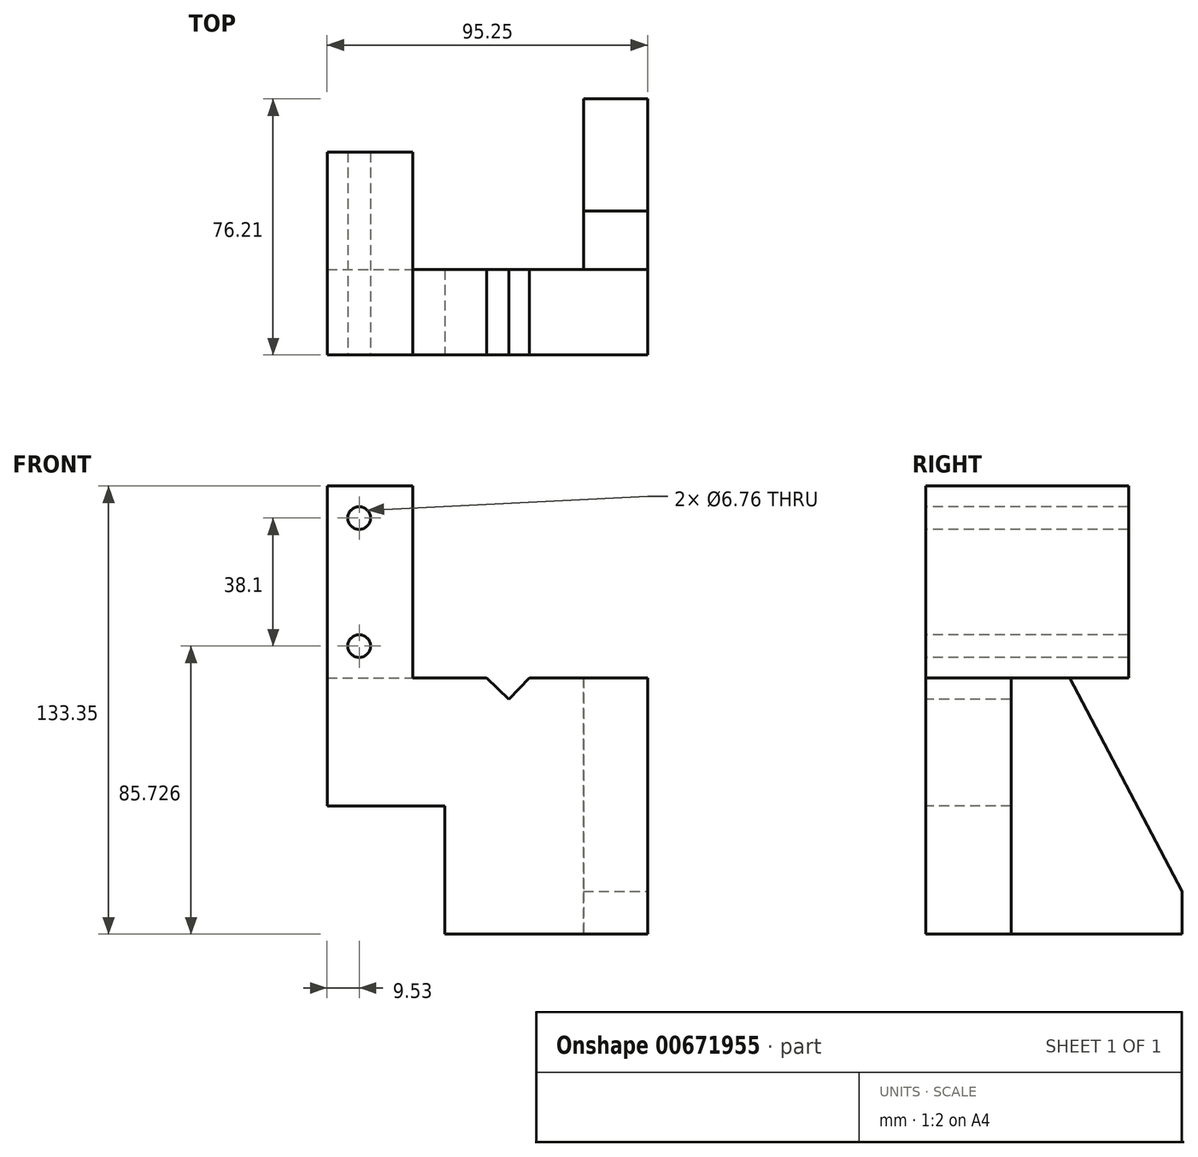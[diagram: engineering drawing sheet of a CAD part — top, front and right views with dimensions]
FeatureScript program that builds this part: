
annotation { "Feature Type Name" : "Feature", "Feature Type Description" : "" }
export const myFeature = defineFeature(function(context is Context, id is Id, definition is map)
    precondition{}
    {
        {
            var Q0;
            Q0=qCreatedBy(makeId("Front.planeOp"),FACE);
            var sketch = newSketch(context, id + "F0", { "sketchPlane" : qUnion([Q0])});
            skLineSegment(sketch, "E0.bottom", {"start": v(-9.53, 39.03) * mm, "end": v(15.87, 39.03) * mm});
            skLineSegment(sketch, "E0.top", {"start": v(-9.52, -18.12) * mm, "end": v(15.88, -18.12) * mm});
            skLineSegment(sketch, "E0.left", {"start": v(-9.53, 39.03) * mm, "end": v(-9.52, -18.12) * mm});
            skLineSegment(sketch, "E0.right", {"start": v(15.87, 39.03) * mm, "end": v(15.88, -18.12) * mm});
            skSolve(sketch);
        }
        {
            var Q0;
            Q0 = qSketchRegion(id + "F0", true);
            extrude(context, id + "F1", {"entities" : qUnion([Q0]), "depth" : 60.32 * mm, "offsetDistance" : 25.4 * mm});
        }
        {
            var Q0;
            Q0=makeQuery(id+"F1.opExtrude","CAP_FACE",FACE,{"disambiguationData":[OSD([sQuery(id+"F0.wireOp",EDGE,"E0.bottom"),sQuery(id+"F0.wireOp",EDGE,"E0.top"),sQuery(id+"F0.wireOp",EDGE,"E0.left"),sQuery(id+"F0.wireOp",EDGE,"E0.right")])],"isStart":false});
            var sketch = newSketch(context, id + "F2", { "sketchPlane" : qUnion([Q0])});
            skPoint(sketch, "E1", {"position": v(0, 29.5) * mm});
            skPoint(sketch, "E2", {"position": v(0, -8.6) * mm});
            skSolve(sketch);
        }
        {
            var Q0;
            Q0=sQuery(id+"F2.wireOp",VERTEX,"E1");
            var Q1;
            Q1=makeQuery(id+"F1.opExtrude","SWEPT_BODY",BODY,{"disambiguationData":[OSD([sQuery(id+"F0.wireOp",EDGE,"E0.bottom"),sQuery(id+"F0.wireOp",EDGE,"E0.top"),sQuery(id+"F0.wireOp",EDGE,"E0.left"),sQuery(id+"F0.wireOp",EDGE,"E0.right")])]});
            hole(context, id + "F3", {"style" : HoleStyle.SIMPLE, "endStyle" : HoleEndStyle.THROUGH, "standardTappedOrClearance" : lookupTablePath({ "standard" : "ANSI", "fit" : "Normal (ASME)", "engagement" : "75%", "pitch" : "20 tpi", "size" : "1/4", "type" : "Clearance" }), "standardBlindInLast" : lookupTablePath({ "fit" : "Free", "standard" : "ANSI", "engagement" : "75%", "pitch" : "20 tpi", "size" : "1/4", "type" : "Clearance" }), "holeDiameter" : 6.76 * mm, "majorDiameter" : 6.35 * mm, "showTappedDepth" : true, "isTappedThrough" : true, "tappedDepth" : 12.7 * mm, "tapClearance" : 3, "locations" : qUnion([Q0]), "scope" : qUnion([Q1])});
        }
        {
            var Q0;
            Q0=makeQuery(id+"F1.opExtrude","CAP_FACE",FACE,{"disambiguationData":[OSD([sQuery(id+"F0.wireOp",EDGE,"E0.bottom"),sQuery(id+"F0.wireOp",EDGE,"E0.top"),sQuery(id+"F0.wireOp",EDGE,"E0.left"),sQuery(id+"F0.wireOp",EDGE,"E0.right")])],"isStart":false});
            var sketch = newSketch(context, id + "F4", { "sketchPlane" : qUnion([Q0])});
            skPoint(sketch, "E3", {"position": v(0, -8.6) * mm});
            skSolve(sketch);
        }
        {
            var Q0;
            Q0=sQuery(id+"F4.wireOp",VERTEX,"E3");
            var Q1;
            Q1=makeQuery(id+"F1.opExtrude","SWEPT_BODY",BODY,{"disambiguationData":[OSD([sQuery(id+"F0.wireOp",EDGE,"E0.bottom"),sQuery(id+"F0.wireOp",EDGE,"E0.top"),sQuery(id+"F0.wireOp",EDGE,"E0.left"),sQuery(id+"F0.wireOp",EDGE,"E0.right")])]});
            hole(context, id + "F5", {"style" : HoleStyle.SIMPLE, "endStyle" : HoleEndStyle.THROUGH, "standardTappedOrClearance" : lookupTablePath({ "standard" : "ANSI", "fit" : "Normal (ASME)", "engagement" : "75%", "pitch" : "20 tpi", "size" : "1/4", "type" : "Clearance" }), "standardBlindInLast" : lookupTablePath({ "fit" : "Free", "standard" : "ANSI", "engagement" : "75%", "pitch" : "20 tpi", "size" : "1/4", "type" : "Clearance" }), "holeDiameter" : 6.76 * mm, "majorDiameter" : 6.35 * mm, "showTappedDepth" : true, "isTappedThrough" : true, "tappedDepth" : 12.7 * mm, "tapClearance" : 3, "locations" : qUnion([Q0]), "scope" : qUnion([Q1])});
        }
        {
            var Q0;
            Q0=makeQuery(id+"F1.opExtrude","SWEPT_FACE",FACE,{"disambiguationData":[OSD([sQuery(id+"F0.wireOp",EDGE,"E0.top")])]});
            var sketch = newSketch(context, id + "F6", { "sketchPlane" : qUnion([Q0])});
            skLineSegment(sketch, "E4.bottom", {"start": v(-9.52, 60.33) * mm, "end": v(85.73, 60.33) * mm});
            skLineSegment(sketch, "E4.top", {"start": v(-9.52, 34.92) * mm, "end": v(85.73, 34.92) * mm});
            skLineSegment(sketch, "E4.left", {"start": v(-9.52, 60.33) * mm, "end": v(-9.52, 34.92) * mm});
            skLineSegment(sketch, "E4.right", {"start": v(85.73, 60.33) * mm, "end": v(85.73, 34.92) * mm});
            skSolve(sketch);
        }
        {
            var Q0;
            Q0 = qSketchRegion(id + "F6", true);
            extrude(context, id + "F7", {"entities" : qUnion([Q0]), "operationType" : NewBodyOperationType.ADD, "depth" : 76.2 * mm, "offsetDistance" : 25.4 * mm});
        }
        {
            var Q0;
            Q0=makeQuery(id+"F7.boolean.opBoolean","MERGE",FACE,{"derivedFrom":[makeQuery(id+"F1.opExtrude","CAP_FACE",FACE,{"disambiguationData":[OSD([sQuery(id+"F0.wireOp",EDGE,"E0.bottom"),sQuery(id+"F0.wireOp",EDGE,"E0.top"),sQuery(id+"F0.wireOp",EDGE,"E0.left"),sQuery(id+"F0.wireOp",EDGE,"E0.right")])],"isStart":false}),makeQuery(id+"F7.opExtrude","SWEPT_FACE",FACE,{"disambiguationData":[OSD([sQuery(id+"F6.wireOp",EDGE,"E4.bottom")])]})]});
            var sketch = newSketch(context, id + "F8", { "sketchPlane" : qUnion([Q0])});
            skLineSegment(sketch, "E5.bottom", {"start": v(-9.52, -56.22) * mm, "end": v(25.4, -56.22) * mm});
            skLineSegment(sketch, "E5.top", {"start": v(-9.52, -94.32) * mm, "end": v(25.4, -94.32) * mm});
            skLineSegment(sketch, "E5.left", {"start": v(-9.52, -56.22) * mm, "end": v(-9.52, -94.32) * mm});
            skLineSegment(sketch, "E5.right", {"start": v(25.4, -56.22) * mm, "end": v(25.4, -94.32) * mm});
            skSolve(sketch);
        }
        {
            var Q0;
            Q0=makeQuery(id+"F8.imprint","IMPRINT",FACE,{"disambiguationData":[TD([[makeQuery(id+"F8.imprint","IMPRINT",EDGE,{"derivedFrom":sQuery(id+"F8.wireOp",EDGE,"E5.bottom")}),-1.0]])]});
            extrude(context, id + "F9", {"entities" : qUnion([Q0]), "operationType" : NewBodyOperationType.REMOVE, "oppositeDirection" : true, "depth" : 50.8 * mm, "offsetDistance" : 25.4 * mm});
        }
        {
            var Q0;
            Q0=makeQuery(id+"F7.boolean.opBoolean","MERGE",FACE,{"derivedFrom":[makeQuery(id+"F1.opExtrude","CAP_FACE",FACE,{"disambiguationData":[OSD([sQuery(id+"F0.wireOp",EDGE,"E0.bottom"),sQuery(id+"F0.wireOp",EDGE,"E0.top"),sQuery(id+"F0.wireOp",EDGE,"E0.left"),sQuery(id+"F0.wireOp",EDGE,"E0.right")])],"isStart":false}),makeQuery(id+"F7.opExtrude","SWEPT_FACE",FACE,{"disambiguationData":[OSD([sQuery(id+"F6.wireOp",EDGE,"E4.bottom")])]})]});
            var sketch = newSketch(context, id + "F10", { "sketchPlane" : qUnion([Q0])});
            skLineSegment(sketch, "E6", {"start": v(29.04, -9.57) * mm, "end": v(44.45, -24.47) * mm});
            skLineSegment(sketch, "E7", {"start": v(44.45, -24.47) * mm, "end": v(57.12, -11.36) * mm});
            skLineSegment(sketch, "E8", {"start": v(29.04, -9.57) * mm, "end": v(57.12, -11.36) * mm});
            skSolve(sketch);
        }
        {
            var Q0;
            Q0 = qSketchRegion(id + "F10", true);
            extrude(context, id + "F11", {"entities" : qUnion([Q0]), "operationType" : NewBodyOperationType.REMOVE, "oppositeDirection" : true, "depth" : 50.8 * mm, "offsetDistance" : 25.4 * mm});
        }
        {
            var Q0;
            Q0=makeQuery(id+"F7.opExtrude","SWEPT_FACE",FACE,{"disambiguationData":[OSD([sQuery(id+"F6.wireOp",EDGE,"E4.right")])]});
            var sketch = newSketch(context, id + "F12", { "sketchPlane" : qUnion([Q0])});
            skLineSegment(sketch, "E9.bottom", {"start": v(-34.92, -18.12) * mm, "end": v(0, -18.12) * mm});
            skLineSegment(sketch, "E9.top", {"start": v(-34.92, -94.32) * mm, "end": v(15.88, -94.32) * mm});
            skLineSegment(sketch, "E9.left", {"start": v(-34.92, -18.12) * mm, "end": v(-34.92, -94.32) * mm});
            skLineSegment(sketch, "E9.right", {"start": v(15.88, -81.62) * mm, "end": v(15.88, -94.32) * mm});
            skLineSegment(sketch, "E10.0", {"start": v(-34.92, -18.12) * mm, "end": v(-17.46, -18.12) * mm});
            skLineSegment(sketch, "E11.0", {"start": v(-34.92, -94.32) * mm, "end": v(-34.92, -18.12) * mm});
            skLineSegment(sketch, "E12", {"start": v(-17.46, -18.12) * mm, "end": v(15.87, -81.62) * mm});
            skSolve(sketch);
        }
        {
            var Q0;
            Q0=makeQuery(id+"F12.imprint","IMPRINT",FACE,{"disambiguationData":[TD([[makeQuery(id+"F12.imprint","IMPRINT",EDGE,{"derivedFrom":sQuery(id+"F12.wireOp",EDGE,"E9.top")}),1.0]])]});
            extrude(context, id + "F13", {"entities" : qUnion([Q0]), "oppositeDirection" : true, "depth" : 19.05 * mm, "offsetDistance" : 25.4 * mm});
        }
    });
